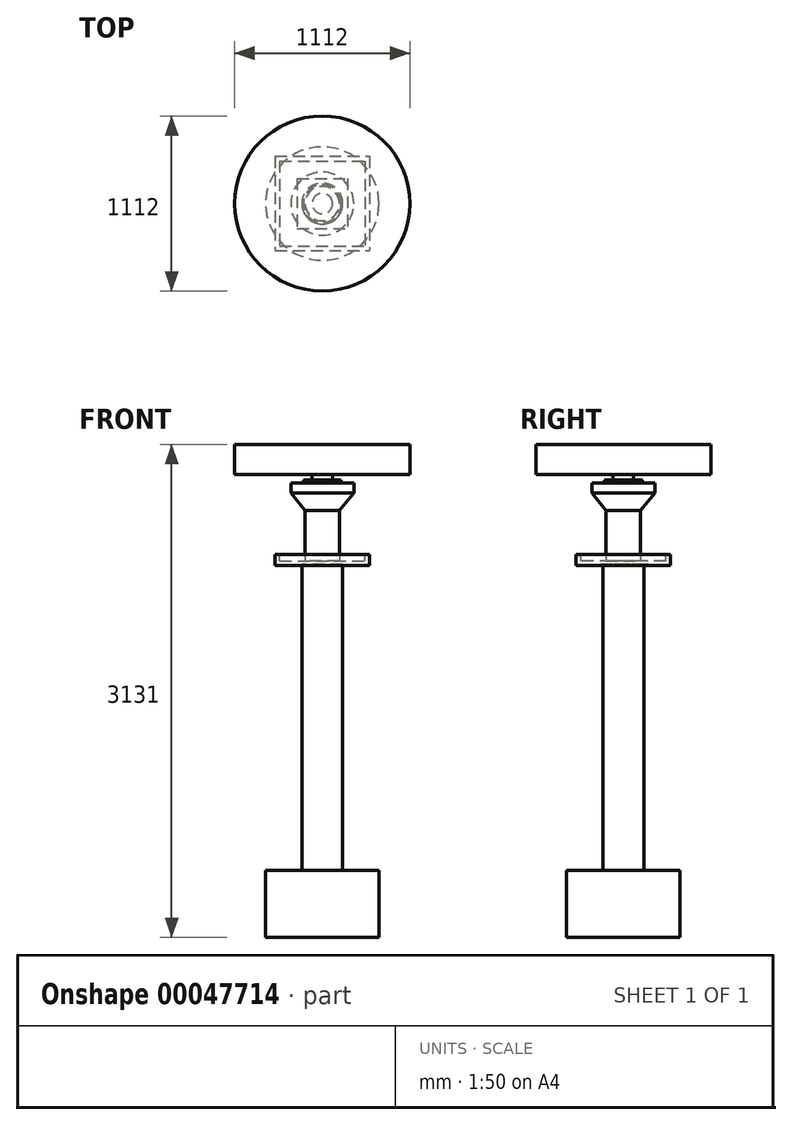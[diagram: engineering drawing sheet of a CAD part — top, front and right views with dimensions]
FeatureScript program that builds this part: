
annotation { "Feature Type Name" : "Feature", "Feature Type Description" : "" }
export const myFeature = defineFeature(function(context is Context, id is Id, definition is map)
    precondition{}
    {
        {
            var Q0;
            Q0=qCreatedBy(makeId("Top.planeOp"),FACE);
            var sketch = newSketch(context, id + "F0", { "sketchPlane" : qUnion([Q0])});
            skLineSegment(sketch, "E0.bottom", {"start": v(0, 0) * mm, "end": v(300, 0) * mm, "construction": true});
            skLineSegment(sketch, "E0.top", {"start": v(0, -300) * mm, "end": v(300, -300) * mm, "construction": true});
            skLineSegment(sketch, "E0.left", {"start": v(0, 0) * mm, "end": v(0, -300) * mm, "construction": true});
            skLineSegment(sketch, "E0.right", {"start": v(300, 0) * mm, "end": v(300, -300) * mm, "construction": true});
            skLineSegment(sketch, "E1.bottom", {"start": v(0, 0) * mm, "end": v(-300, 0) * mm, "construction": true});
            skLineSegment(sketch, "E1.top", {"start": v(0, 300) * mm, "end": v(-300, 300) * mm, "construction": true});
            skLineSegment(sketch, "E1.left", {"start": v(0, 0) * mm, "end": v(0, 300) * mm, "construction": true});
            skLineSegment(sketch, "E1.right", {"start": v(-300, 0) * mm, "end": v(-300, 300) * mm, "construction": true});
            skLineSegment(sketch, "E2.bottom", {"start": v(-300, 300) * mm, "end": v(300, 300) * mm});
            skLineSegment(sketch, "E2.top", {"start": v(-300, -300) * mm, "end": v(300, -300) * mm});
            skLineSegment(sketch, "E2.left", {"start": v(-300, 300) * mm, "end": v(-300, -300) * mm});
            skLineSegment(sketch, "E2.right", {"start": v(300, 300) * mm, "end": v(300, -300) * mm});
            skLineSegment(sketch, "E3.bottom", {"start": v(-300, 300) * mm, "end": v(-160, 300) * mm, "construction": true});
            skLineSegment(sketch, "E3.top", {"start": v(-300, 160) * mm, "end": v(-160, 160) * mm, "construction": true});
            skLineSegment(sketch, "E3.left", {"start": v(-300, 300) * mm, "end": v(-300, 160) * mm, "construction": true});
            skLineSegment(sketch, "E3.right", {"start": v(-160, 300) * mm, "end": v(-160, 160) * mm, "construction": true});
            skLineSegment(sketch, "E4.bottom", {"start": v(300, -300) * mm, "end": v(160, -300) * mm, "construction": true});
            skLineSegment(sketch, "E4.top", {"start": v(300, -160) * mm, "end": v(160, -160) * mm, "construction": true});
            skLineSegment(sketch, "E4.left", {"start": v(300, -300) * mm, "end": v(300, -160) * mm, "construction": true});
            skLineSegment(sketch, "E4.right", {"start": v(160, -300) * mm, "end": v(160, -160) * mm, "construction": true});
            skLineSegment(sketch, "E5.bottom", {"start": v(-160, 160) * mm, "end": v(160, 160) * mm});
            skLineSegment(sketch, "E5.top", {"start": v(-160, -160) * mm, "end": v(160, -160) * mm});
            skLineSegment(sketch, "E5.left", {"start": v(-160, 160) * mm, "end": v(-160, -160) * mm});
            skLineSegment(sketch, "E5.right", {"start": v(160, 160) * mm, "end": v(160, -160) * mm});
            skSolve(sketch);
        }
        {
            var Q0;
            Q0 = qSketchRegion(id + "F0", true);
            extrude(context, id + "F1", {"entities" : qUnion([Q0]), "depth" : 5 * mm});
        }
        {
            var Q0;
            Q0=makeQuery(id+"F1.opExtrude","CAP_FACE",FACE,{"disambiguationData":[OSD([sQuery(id+"F0.wireOp",EDGE,"E2.bottom"),sQuery(id+"F0.wireOp",EDGE,"E2.top"),sQuery(id+"F0.wireOp",EDGE,"E2.left"),sQuery(id+"F0.wireOp",EDGE,"E2.right"),sQuery(id+"F0.wireOp",EDGE,"E5.bottom"),sQuery(id+"F0.wireOp",EDGE,"E5.top"),sQuery(id+"F0.wireOp",EDGE,"E5.left"),sQuery(id+"F0.wireOp",EDGE,"E5.right")])],"isStart":false});
            var sketch = newSketch(context, id + "F2", { "sketchPlane" : qUnion([Q0])});
            skLineSegment(sketch, "E6.0", {"start": v(-300, 300) * mm, "end": v(300, 300) * mm});
            skLineSegment(sketch, "E7.0", {"start": v(-300, 300) * mm, "end": v(-300, -300) * mm});
            skLineSegment(sketch, "E8.0", {"start": v(-300, -300) * mm, "end": v(300, -300) * mm});
            skLineSegment(sketch, "E9.0", {"start": v(300, 300) * mm, "end": v(300, -300) * mm});
            skSolve(sketch);
        }
        {
            var Q0;
            Q0 = qSketchRegion(id + "F2", true);
            extrude(context, id + "F3", {"entities" : qUnion([Q0]), "operationType" : NewBodyOperationType.ADD, "depth" : 65 * mm});
        }
        {
            var Q0;
            Q0=makeQuery(id+"F3.opExtrude","CAP_FACE",FACE,{"disambiguationData":[OSD([sQuery(id+"F2.wireOp",EDGE,"E6.0"),sQuery(id+"F2.wireOp",EDGE,"E8.0"),sQuery(id+"F2.wireOp",EDGE,"E7.0"),sQuery(id+"F2.wireOp",EDGE,"E9.0")])],"isStart":false});
            var sketch = newSketch(context, id + "F4", { "sketchPlane" : qUnion([Q0])});
            skPoint(sketch, "E10.0", {"position": v(-300, 300) * mm});
            skPoint(sketch, "E10.1", {"position": v(300, 300) * mm});
            skLineSegment(sketch, "E11.bottom", {"start": v(-300, 300) * mm, "end": v(-270, 300) * mm, "construction": true});
            skLineSegment(sketch, "E11.top", {"start": v(-300, 270) * mm, "end": v(-270, 270) * mm, "construction": true});
            skLineSegment(sketch, "E11.left", {"start": v(-300, 300) * mm, "end": v(-300, 270) * mm, "construction": true});
            skLineSegment(sketch, "E11.right", {"start": v(-270, 300) * mm, "end": v(-270, 270) * mm, "construction": true});
            skLineSegment(sketch, "E12.bottom", {"start": v(300, -300) * mm, "end": v(270, -300) * mm, "construction": true});
            skLineSegment(sketch, "E12.top", {"start": v(300, -270) * mm, "end": v(270, -270) * mm, "construction": true});
            skLineSegment(sketch, "E12.left", {"start": v(300, -300) * mm, "end": v(300, -270) * mm, "construction": true});
            skLineSegment(sketch, "E12.right", {"start": v(270, -300) * mm, "end": v(270, -270) * mm, "construction": true});
            skLineSegment(sketch, "E13.bottom", {"start": v(-270, 270) * mm, "end": v(270, 270) * mm});
            skLineSegment(sketch, "E13.top", {"start": v(-270, -270) * mm, "end": v(270, -270) * mm});
            skLineSegment(sketch, "E13.left", {"start": v(-270, 270) * mm, "end": v(-270, -270) * mm});
            skLineSegment(sketch, "E13.right", {"start": v(270, 270) * mm, "end": v(270, -270) * mm});
            skSolve(sketch);
        }
        {
            var Q0;
            Q0 = qSketchRegion(id + "F4", true);
            extrude(context, id + "F5", {"entities" : qUnion([Q0]), "operationType" : NewBodyOperationType.REMOVE, "oppositeDirection" : true, "depth" : 40 * mm});
        }
        {
            var Q0;
            Q0=makeQuery(id+"F5.boolean.opBoolean","COPY",FACE,{"derivedFrom":makeQuery(id+"F5.opExtrude","CAP_FACE",FACE,{"disambiguationData":[OSD([sQuery(id+"F4.wireOp",EDGE,"E13.bottom"),sQuery(id+"F4.wireOp",EDGE,"E13.top"),sQuery(id+"F4.wireOp",EDGE,"E13.left"),sQuery(id+"F4.wireOp",EDGE,"E13.right")])],"isStart":false})});
            var sketch = newSketch(context, id + "F6", { "sketchPlane" : qUnion([Q0])});
            skCircle(sketch, "E14", {"center": v(0, 0) * mm, "radius": 109 * mm});
            skSolve(sketch);
        }
        {
            var Q0;
            Q0 = qSketchRegion(id + "F6", true);
            extrude(context, id + "F7", {"entities" : qUnion([Q0]), "operationType" : NewBodyOperationType.ADD, "depth" : 320 * mm});
        }
        {
            var Q0;
            Q0=makeQuery(id+"F7.opExtrude","CAP_FACE",FACE,{"disambiguationData":[OSD([sQuery(id+"F6.wireOp",EDGE,"E14")])],"isStart":false});
            var sketch = newSketch(context, id + "F8", { "sketchPlane" : qUnion([Q0])});
            skCircle(sketch, "E15.0", {"center": v(0, 0) * mm, "radius": 109 * mm});
            skSolve(sketch);
        }
        {
            var Q0;
            Q0=makeQuery(id+"F8.imprint","IMPRINT",FACE,{"disambiguationData":[TD([[makeQuery(id+"F8.imprint","IMPRINT",EDGE,{"derivedFrom":sQuery(id+"F8.wireOp",EDGE,"E15.0")}),1.0]])]});
            cPlane(context, id + "F9", {"entities" : qUnion([Q0]), "cplaneType" : CPlaneType.OFFSET, "offset" : 110 * mm, "width" : 150 * mm, "height" : 150 * mm});
        }
        {
            var Q0;
            Q0=qCreatedBy(id+"F9.planeOp",FACE);
            var sketch = newSketch(context, id + "F10", { "sketchPlane" : qUnion([Q0])});
            skCircle(sketch, "E16", {"center": v(0, 0) * mm, "radius": 200 * mm});
            skSolve(sketch);
        }
        {
            var Q1;
            Q1=makeQuery(id+"F8.imprint","IMPRINT",FACE,{"disambiguationData":[TD([[makeQuery(id+"F8.imprint","IMPRINT",EDGE,{"derivedFrom":sQuery(id+"F8.wireOp",EDGE,"E15.0")}),1.0]])]});
            var Q2;
            Q2=makeQuery(id+"F10.imprint","IMPRINT",FACE,{"disambiguationData":[TD([[makeQuery(id+"F10.imprint","IMPRINT",EDGE,{"derivedFrom":sQuery(id+"F10.wireOp",EDGE,"E16")}),1.0]])]});
            loft(context, id + "F11", {"operationType" : NewBodyOperationType.ADD, "sheetProfilesArray" : [{ "sheetProfileEntities" : qUnion([Q1]) }, { "sheetProfileEntities" : qUnion([Q2]) }]});
        }
        {
            var Q0;
            Q0=makeQuery(id+"F11.opLoft","CAP_FACE",FACE,{"disambiguationData":[OSD([makeQuery(id+"F10.imprint","IMPRINT",FACE,{"disambiguationData":[TD([[makeQuery(id+"F10.imprint","IMPRINT",EDGE,{"derivedFrom":sQuery(id+"F10.wireOp",EDGE,"E16")}),1.0]])]})])],"isStart":true});
            var sketch = newSketch(context, id + "F12", { "sketchPlane" : qUnion([Q0])});
            skCircle(sketch, "E17.0", {"center": v(0, 0) * mm, "radius": 200 * mm});
            skSolve(sketch);
        }
        {
            var Q0;
            Q0 = qSketchRegion(id + "F12", true);
            extrude(context, id + "F13", {"entities" : qUnion([Q0]), "operationType" : NewBodyOperationType.ADD, "depth" : 65 * mm});
        }
        {
            var Q0;
            Q0=makeQuery(id+"F13.opExtrude","CAP_FACE",FACE,{"disambiguationData":[OSD([sQuery(id+"F12.wireOp",EDGE,"E17.0")])],"isStart":false});
            var sketch = newSketch(context, id + "F14", { "sketchPlane" : qUnion([Q0])});
            skCircle(sketch, "E18", {"center": v(0, 0) * mm, "radius": 120 * mm});
            skSolve(sketch);
        }
        {
            var Q0;
            Q0 = qSketchRegion(id + "F14", true);
            extrude(context, id + "F15", {"entities" : qUnion([Q0]), "operationType" : NewBodyOperationType.ADD, "depth" : 18 * mm});
        }
        {
            var Q0;
            Q0=makeQuery(id+"F15.opExtrude","CAP_FACE",FACE,{"disambiguationData":[OSD([sQuery(id+"F14.wireOp",EDGE,"E18")])],"isStart":false});
            var sketch = newSketch(context, id + "F16", { "sketchPlane" : qUnion([Q0])});
            skCircle(sketch, "E19", {"center": v(0, 0) * mm, "radius": 65 * mm});
            skSolve(sketch);
        }
        {
            var Q0;
            Q0 = qSketchRegion(id + "F16", true);
            extrude(context, id + "F17", {"entities" : qUnion([Q0]), "operationType" : NewBodyOperationType.ADD, "depth" : 35 * mm});
        }
        {
            var Q0;
            Q0=makeQuery(id+"F17.opExtrude","CAP_FACE",FACE,{"disambiguationData":[OSD([sQuery(id+"F16.wireOp",EDGE,"E19")])],"isStart":false});
            var sketch = newSketch(context, id + "F18", { "sketchPlane" : qUnion([Q0])});
            skCircle(sketch, "E20", {"center": v(0, 0) * mm, "radius": 556 * mm});
            skSolve(sketch);
        }
        {
            var Q0;
            Q0 = qSketchRegion(id + "F18", true);
            extrude(context, id + "F19", {"entities" : qUnion([Q0]), "operationType" : NewBodyOperationType.ADD, "depth" : 190 * mm});
        }
        {
            var Q0;
            Q0=makeQuery(id+"F3.opExtrude","CAP_FACE",FACE,{"disambiguationData":[OSD([sQuery(id+"F2.wireOp",EDGE,"E6.0"),sQuery(id+"F2.wireOp",EDGE,"E8.0"),sQuery(id+"F2.wireOp",EDGE,"E7.0"),sQuery(id+"F2.wireOp",EDGE,"E9.0")])],"isStart":true});
            var sketch = newSketch(context, id + "F20", { "sketchPlane" : qUnion([Q0])});
            skCircle(sketch, "E21", {"center": v(0, 0) * mm, "radius": 130 * mm});
            skSolve(sketch);
        }
        {
            var Q0;
            Q0 = qSketchRegion(id + "F20", true);
            extrude(context, id + "F21", {"entities" : qUnion([Q0]), "operationType" : NewBodyOperationType.ADD, "depth" : 1942 * mm});
        }
        {
            var Q0;
            Q0=makeQuery(id+"F21.opExtrude","CAP_FACE",FACE,{"disambiguationData":[OSD([sQuery(id+"F20.wireOp",EDGE,"E21")])],"isStart":false});
            var sketch = newSketch(context, id + "F22", { "sketchPlane" : qUnion([Q0])});
            skCircle(sketch, "E22", {"center": v(0, 0) * mm, "radius": 360 * mm});
            skSolve(sketch);
        }
        {
            var Q0;
            Q0 = qSketchRegion(id + "F22", true);
            extrude(context, id + "F23", {"entities" : qUnion([Q0]), "operationType" : NewBodyOperationType.ADD, "depth" : 426 * mm});
        }
    });
